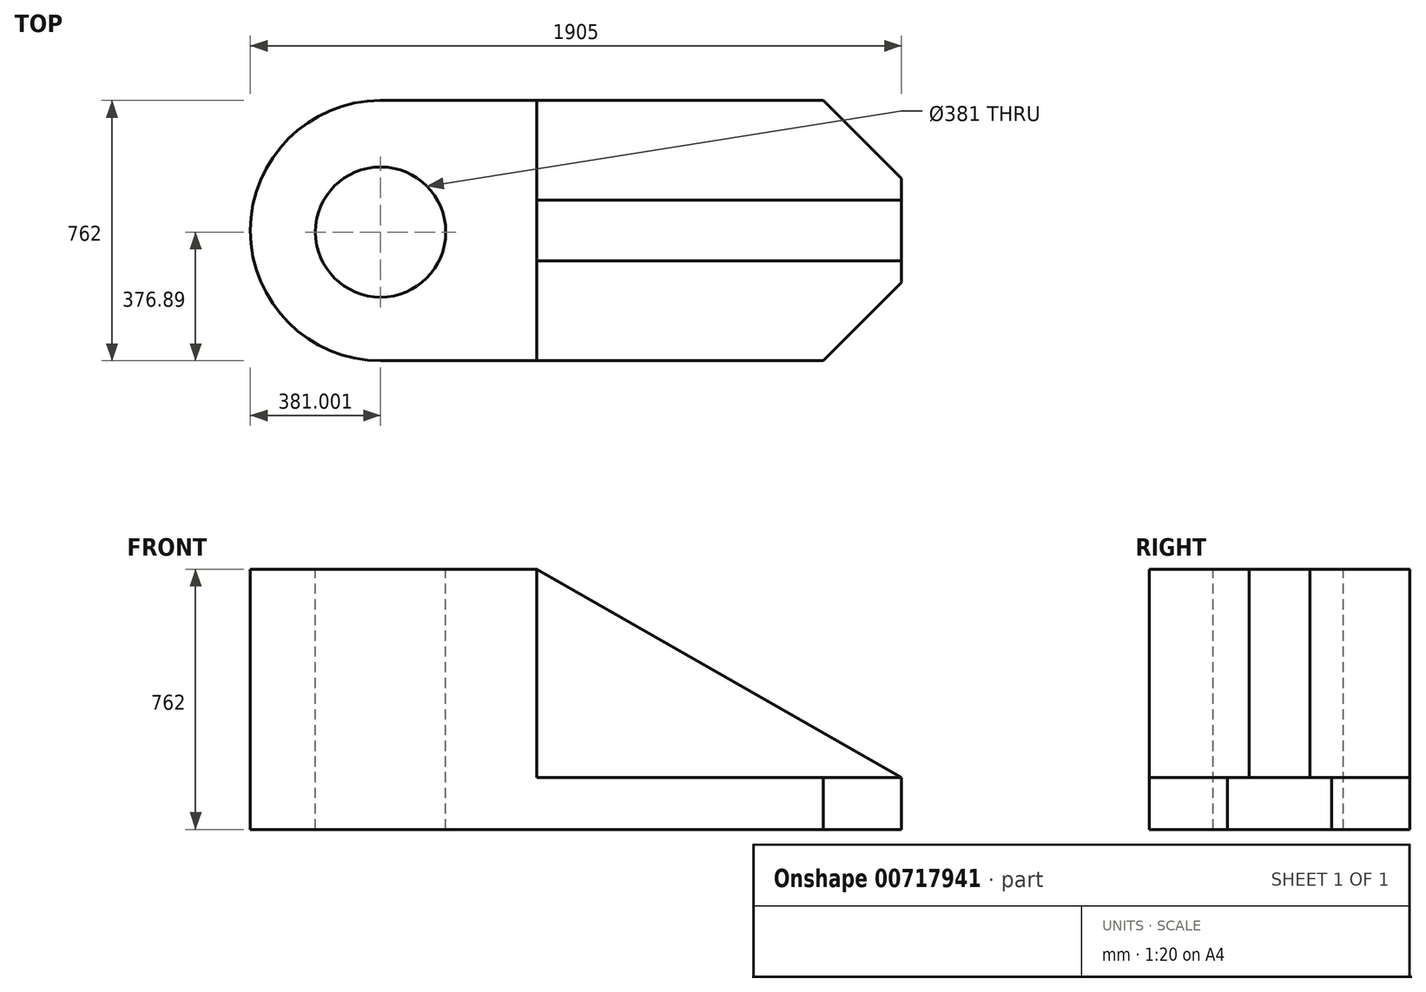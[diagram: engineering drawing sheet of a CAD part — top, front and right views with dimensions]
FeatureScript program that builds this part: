
annotation { "Feature Type Name" : "Feature", "Feature Type Description" : "" }
export const myFeature = defineFeature(function(context is Context, id is Id, definition is map)
    precondition{}
    {
        {
            var Q0;
            Q0=qCreatedBy(makeId("Top.planeOp"),FACE);
            var sketch = newSketch(context, id + "F0", { "sketchPlane" : qUnion([Q0])});
            skArc(sketch, "E0", {"start": v(-68.56, 385.11) * mm, "mid": v(-449.56, 4.11) * mm, "end": v(-68.56, -376.89) * mm});
            skLineSegment(sketch, "E1", {"start": v(-68.56, -376.89) * mm, "end": v(1455.44, -376.89) * mm});
            skLineSegment(sketch, "E2", {"start": v(1455.44, -376.89) * mm, "end": v(1455.44, 385.11) * mm});
            skLineSegment(sketch, "E3", {"start": v(1455.44, 385.11) * mm, "end": v(-68.56, 385.11) * mm});
            skSolve(sketch);
        }
        {
            var Q0;
            Q0=makeQuery(id+"F0.imprint","IMPRINT",FACE,{"disambiguationData":[TD([[makeQuery(id+"F0.imprint","IMPRINT",EDGE,{"derivedFrom":sQuery(id+"F0.wireOp",EDGE,"E0")}),1.0]])]});
            extrude(context, id + "F1", {"entities" : qUnion([Q0]), "depth" : 152.4 * mm, "offsetDistance" : 25.4 * mm});
        }
        {
            var Q0;
            Q0=makeQuery(id+"F1.opExtrude","CAP_FACE",FACE,{"disambiguationData":[OSD([sQuery(id+"F0.wireOp",EDGE,"E0"),sQuery(id+"F0.wireOp",EDGE,"E1"),sQuery(id+"F0.wireOp",EDGE,"E2"),sQuery(id+"F0.wireOp",EDGE,"E3")])],"isStart":false});
            var sketch = newSketch(context, id + "F2", { "sketchPlane" : qUnion([Q0])});
            skArc(sketch, "E4", {"start": v(-68.56, 385.11) * mm, "mid": v(-449.56, 4.11) * mm, "end": v(-68.56, -376.89) * mm});
            skLineSegment(sketch, "E5.bottom", {"start": v(-68.56, 385.11) * mm, "end": v(388.64, 385.11) * mm});
            skLineSegment(sketch, "E5.top", {"start": v(-68.56, -376.89) * mm, "end": v(388.64, -376.89) * mm});
            skLineSegment(sketch, "E5.right", {"start": v(388.64, 385.11) * mm, "end": v(388.64, -376.89) * mm});
            skSolve(sketch);
        }
        {
            var Q0;
            Q0=makeQuery(id+"F2.imprint","IMPRINT",FACE,{"disambiguationData":[TD([[makeQuery(id+"F2.imprint","IMPRINT",EDGE,{"derivedFrom":sQuery(id+"F2.wireOp",EDGE,"E4")}),1.0]])]});
            extrude(context, id + "F3", {"entities" : qUnion([Q0]), "operationType" : NewBodyOperationType.ADD, "depth" : 609.6 * mm, "offsetDistance" : 25.4 * mm});
        }
        {
            var Q0;
            Q0=makeQuery(id+"F3.opExtrude","SWEPT_FACE",FACE,{"disambiguationData":[OSD([sQuery(id+"F2.wireOp",EDGE,"E5.right")])]});
            var sketch = newSketch(context, id + "F4", { "sketchPlane" : qUnion([Q0])});
            skLineSegment(sketch, "E6.bottom", {"start": v(-84.79, 762) * mm, "end": v(93.01, 762) * mm});
            skLineSegment(sketch, "E6.top", {"start": v(-84.79, 152.4) * mm, "end": v(93.01, 152.4) * mm});
            skLineSegment(sketch, "E6.left", {"start": v(-84.79, 762) * mm, "end": v(-84.79, 152.4) * mm});
            skLineSegment(sketch, "E6.right", {"start": v(93.01, 762) * mm, "end": v(93.01, 152.4) * mm});
            skSolve(sketch);
        }
        {
            var Q0;
            Q0=makeQuery(id+"F4.imprint","IMPRINT",FACE,{"disambiguationData":[TD([[makeQuery(id+"F4.imprint","IMPRINT",EDGE,{"derivedFrom":sQuery(id+"F4.wireOp",EDGE,"E6.bottom")}),1.0]])]});
            extrude(context, id + "F5", {"entities" : qUnion([Q0]), "operationType" : NewBodyOperationType.ADD, "depth" : 1066.8 * mm, "offsetDistance" : 25.4 * mm});
        }
        {
            var Q0;
            Q0=makeQuery(id+"F5.opExtrude","SWEPT_FACE",FACE,{"disambiguationData":[OSD([sQuery(id+"F4.wireOp",EDGE,"E6.left")])]});
            var sketch = newSketch(context, id + "F6", { "sketchPlane" : qUnion([Q0])});
            skLineSegment(sketch, "E7", {"start": v(388.64, 762) * mm, "end": v(1455.44, 152.4) * mm});
            skLineSegment(sketch, "E8", {"start": v(1455.44, 152.4) * mm, "end": v(1455.44, 762) * mm});
            skLineSegment(sketch, "E9", {"start": v(1455.44, 762) * mm, "end": v(388.64, 762) * mm});
            skSolve(sketch);
        }
        {
            var Q0;
            Q0=makeQuery(id+"F6.imprint","IMPRINT",FACE,{"disambiguationData":[TD([[makeQuery(id+"F6.imprint","IMPRINT",EDGE,{"derivedFrom":sQuery(id+"F6.wireOp",EDGE,"E7")}),1.0]])]});
            extrude(context, id + "F7", {"entities" : qUnion([Q0]), "operationType" : NewBodyOperationType.REMOVE, "oppositeDirection" : true, "depth" : 177.8 * mm, "offsetDistance" : 25.4 * mm});
        }
        {
            var Q0;
            {var subQ0=sQuery(id+"F0.wireOp",EDGE,"E2");var subQ1=sQuery(id+"F0.wireOp",EDGE,"E3");Q0=makeQuery(id+"F5.boolean.opBoolean","SPLIT",FACE,{"disambiguationData":[TD([makeQuery(id+"F1.opExtrude","SWEPT_FACE",FACE,{"disambiguationData":[OSD([subQ1])]})])],"derivedFrom":makeQuery(id+"F1.opExtrude","CAP_FACE",FACE,{"disambiguationData":[OSD([sQuery(id+"F0.wireOp",EDGE,"E0"),sQuery(id+"F0.wireOp",EDGE,"E1"),subQ0,subQ1])],"isStart":false})});}
            var sketch = newSketch(context, id + "F8", { "sketchPlane" : qUnion([Q0])});
            skLineSegment(sketch, "E10", {"start": v(1455.44, 385.11) * mm, "end": v(1455.44, 156.51) * mm});
            skLineSegment(sketch, "E11", {"start": v(1455.44, 156.51) * mm, "end": v(1226.84, 385.11) * mm});
            skLineSegment(sketch, "E12", {"start": v(1226.84, 385.11) * mm, "end": v(1455.44, 385.11) * mm});
            skSolve(sketch);
        }
        {
            var Q0;
            {var subQ0=sQuery(id+"F0.wireOp",EDGE,"E2");var subQ1=sQuery(id+"F0.wireOp",EDGE,"E1");Q0=makeQuery(id+"F5.boolean.opBoolean","SPLIT",FACE,{"disambiguationData":[TD([makeQuery(id+"F1.opExtrude","SWEPT_FACE",FACE,{"disambiguationData":[OSD([subQ1])]})])],"derivedFrom":makeQuery(id+"F1.opExtrude","CAP_FACE",FACE,{"disambiguationData":[OSD([sQuery(id+"F0.wireOp",EDGE,"E0"),subQ1,subQ0,sQuery(id+"F0.wireOp",EDGE,"E3")])],"isStart":false})});}
            var sketch = newSketch(context, id + "F9", { "sketchPlane" : qUnion([Q0])});
            skLineSegment(sketch, "E13", {"start": v(1455.44, -376.89) * mm, "end": v(1455.44, -148.29) * mm});
            skLineSegment(sketch, "E14", {"start": v(1455.44, -148.29) * mm, "end": v(1226.84, -376.89) * mm});
            skLineSegment(sketch, "E15", {"start": v(1226.84, -376.89) * mm, "end": v(1455.44, -376.89) * mm});
            skSolve(sketch);
        }
        {
            var Q0;
            Q0=makeQuery(id+"F8.imprint","IMPRINT",FACE,{"disambiguationData":[TD([[makeQuery(id+"F8.imprint","IMPRINT",EDGE,{"derivedFrom":sQuery(id+"F8.wireOp",EDGE,"E10")}),1.0]])]});
            var Q1;
            Q1=makeQuery(id+"F9.imprint","IMPRINT",FACE,{"disambiguationData":[TD([[makeQuery(id+"F9.imprint","IMPRINT",EDGE,{"derivedFrom":sQuery(id+"F9.wireOp",EDGE,"E13")}),1.0]])]});
            extrude(context, id + "F10", {"entities" : qUnion([Q0, Q1]), "operationType" : NewBodyOperationType.REMOVE, "oppositeDirection" : true, "depth" : 152.4 * mm, "offsetDistance" : 25.4 * mm});
        }
        {
            var Q0;
            Q0=makeQuery(id+"F5.boolean.opBoolean","MERGE",FACE,{"derivedFrom":[makeQuery(id+"F3.opExtrude","CAP_FACE",FACE,{"disambiguationData":[OSD([sQuery(id+"F2.wireOp",EDGE,"E4"),sQuery(id+"F2.wireOp",EDGE,"E5.bottom"),sQuery(id+"F2.wireOp",EDGE,"E5.top"),sQuery(id+"F2.wireOp",EDGE,"E5.right")])],"isStart":false}),makeQuery(id+"F5.opExtrude","SWEPT_FACE",FACE,{"disambiguationData":[OSD([sQuery(id+"F4.wireOp",EDGE,"E6.bottom")])]})]});
            var sketch = newSketch(context, id + "F11", { "sketchPlane" : qUnion([Q0])});
            skCircle(sketch, "E16", {"center": v(-68.56, 0) * mm, "radius": 190.5 * mm});
            skSolve(sketch);
        }
        {
            var Q0;
            Q0=makeQuery(id+"F11.imprint","IMPRINT",FACE,{"disambiguationData":[TD([[makeQuery(id+"F11.imprint","IMPRINT",EDGE,{"derivedFrom":sQuery(id+"F11.wireOp",EDGE,"E16")}),1.0]])]});
            extrude(context, id + "F12", {"entities" : qUnion([Q0]), "operationType" : NewBodyOperationType.REMOVE, "oppositeDirection" : true, "depth" : 762 * mm, "offsetDistance" : 25.4 * mm});
        }
    });
